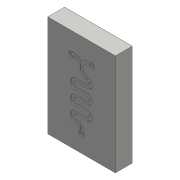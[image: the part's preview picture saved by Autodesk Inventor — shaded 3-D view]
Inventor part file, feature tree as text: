
AUTODESK INVENTOR PART (.ipt)
format: ipt  version: 2016 (Build 200138000, 138)  size: 155,136 bytes
history: native  units: mm
features: extrude x3, sketch x2, other x1
ambient origin geometry x8: Origin, YZ Plane, XZ Plane, XY Plane, X Axis, Y Axis, Z Axis, Center Point
bodies: Body1 (feature_tree)
feature tree (6):
  other  "Sólido1"
  sketch  "Boceto1"  dims[d1=5.0mm d2=0.0mm d3=0.2mm d4=0.0mm]
  extrude  "Extrusión1"  Depth=0.2mm TaperAngle=0.0deg
  extrude  "Extrusión2"  Depth=0.2mm
  extrude  "Extrusión3"  Depth=0.2mm
  sketch  "Boceto3"  dims[d5=0.7mm d6=0.7mm d7=0.7mm d8=0.2mm d9=0.0mm]
